# Revit family: Plate_System_Water_Coolers-Zurn_Z1218
name_source: partatom
category: Plumbing Fixtures
units: mm (PartAtom-declared; Revit-internal decimal feet)

## family parameters
Cut with Voids When Loaded = No
Host = Face
Maintain Annotation Orientation = No
OmniClass Number = 23.45.55.11
OmniClass Title = Sanitary Components
Part Type = Normal
Room Calculation Point = No
Round Connector Dimension = Use Radius
Shared = No

## types (2) — shared parameters
Assembly Code = D2010210
Body = Steel - Zurn - Stainless - Type - 304
Bracket = Steel - Zurn - Stainless - A.R.E Coated - Type - 304
CW Connection = No
Coupling = Plastic - Zurn - White
Description = COUPLING TYPE SYSTEM WALL URINAL / SERVICE SINK
Flush Flow = 0.0 L/s
HW Connection = No
Manufacturer = Zurn Water, LLC
Manufacturer Brand = Zurn
Modified Date = 11/21/2025
Product Documentation Link = https://files.zurn.com
Product Page URL = https://www.zurn.com
Product data url = https://bimobject.com
URL = http://www.zurn.com
Vent Connection = No
WFU = 1
Waste Connection = Yes
zero-valued in all types: CWFU, Default Elevation, HWFU

## per-type parameters (varying)
| type | Coupling Diameter | Coupling Radius | Outlet Nominal Diameter | Outlet Nominal Radius |
| Z1218-3 | 5 " | 2.5 " | 3 " | 1.5 " |
| Z1218-4 | 0 " | 0 " | 4 " | 2 " |

note: column(s) folded — value = type name in every type: Model

## geometry (parser evidence)
native form markers: Sweep x8
no freeform markers — native parametric forms only
